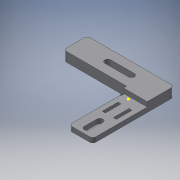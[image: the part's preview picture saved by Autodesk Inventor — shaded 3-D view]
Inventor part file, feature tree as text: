
AUTODESK INVENTOR PART (.ipt)
format: ipt  version: 2019 (Build 230136000, 136)  size: 205,824 bytes
history: native  units: in
note: dims shown in document units (in); Inventor stores cm internally (conversion verified against a paired STEP export)
features: sketch x8, extrude x7, fillet x2, projected_geometry x1
ambient origin geometry x8: Origin, YZ Plane, XZ Plane, XY Plane, X Axis, Y Axis, Z Axis, Center Point
bodies: Solid1 (feature_tree)
feature tree (18):
  extrude  "Extrusion1"  Depth=0.1181in TaperAngle=0.0deg
  extrude  "Extrusion3"  Depth=0.3937in
  extrude  "Extrusion4"  Depth=0.0787in TaperAngle=0.0deg
  extrude  "Extrusion5"  Depth=0.5906in
  fillet  "Fillet2"  Radius=1.1811in
  extrude  "Extrusion6"  Depth=0.0787in TaperAngle=0.0deg
  sketch  "Sketch10"  dims[d36=0.1495in d37=0.315in]
  extrude  "Extrusion7"  Depth=0.1495in
  extrude  "Extrusion8"  Depth=0.1575in
  fillet  "Fillet3"  Radius=0.0787in
  sketch  "Sketch1"  dims[d2=0.1181in d3=0.0in d16=0.1181in d17=0.0in]
  sketch  "Sketch4"  dims[d24=0.0787in d25=0.3937in]
  sketch  "Sketch5"  dims[d26=0.2756in d28=0.0787in d29=0.0in]
  sketch  "Sketch6"  dims[d30=0.5906in d31=0.8465in d32=1.1811in]
  projected_geometry  "Projected Loop1"
  sketch  "Sketch8"  dims[d33=0.1495in d34=0.0787in d35=0.0in]
  sketch  "Sketch11"  dims[d61=0.5906in d68=0.1575in d69=0.0787in]
  sketch  "Sketch12"  dims[d72=0.0394in d73=0.0in d74=0.0197in d75=0.0787in d85=0.1495in d86=0.5906in d87=0.3937in d88=0.0in d89=0.0787in d90=0.2559in d91=1.5748in d92=0.4724in d93=0.51in d94=0.1875in d95=0.0in d96=0.315in d97=0.0787in]
